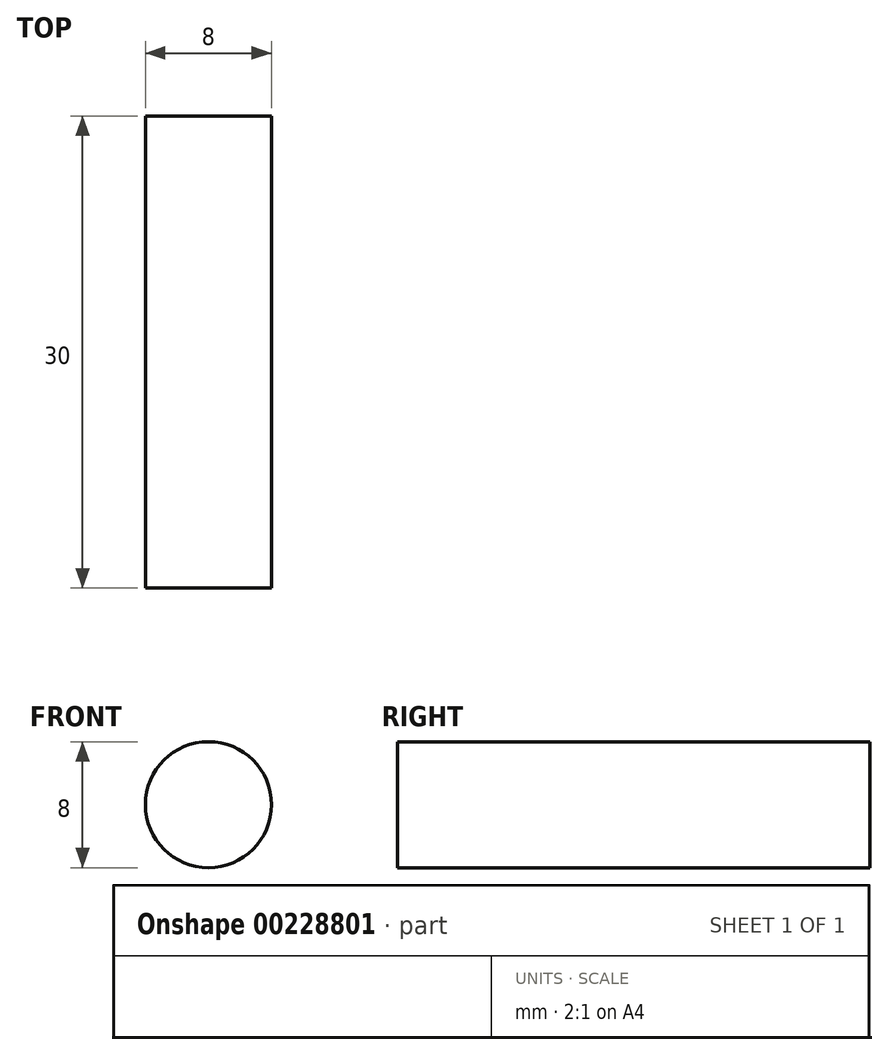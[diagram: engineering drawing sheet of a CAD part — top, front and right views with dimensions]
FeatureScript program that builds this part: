
annotation { "Feature Type Name" : "Feature", "Feature Type Description" : "" }
export const myFeature = defineFeature(function(context is Context, id is Id, definition is map)
    precondition{}
    {
        {
            var Q0;
            Q0=qCreatedBy(makeId("Front.planeOp"),FACE);
            var sketch = newSketch(context, id + "F0", { "sketchPlane" : qUnion([Q0])});
            skCircle(sketch, "E0", {"center": v(0, 0) * mm, "radius": 4 * mm});
            skSolve(sketch);
        }
        {
            var Q0;
            Q0 = qSketchRegion(id + "F0", true);
            extrude(context, id + "F1", {"entities" : qUnion([Q0]), "endBound" : BoundingType.SYMMETRIC, "depth" : 30 * mm});
        }
    });
